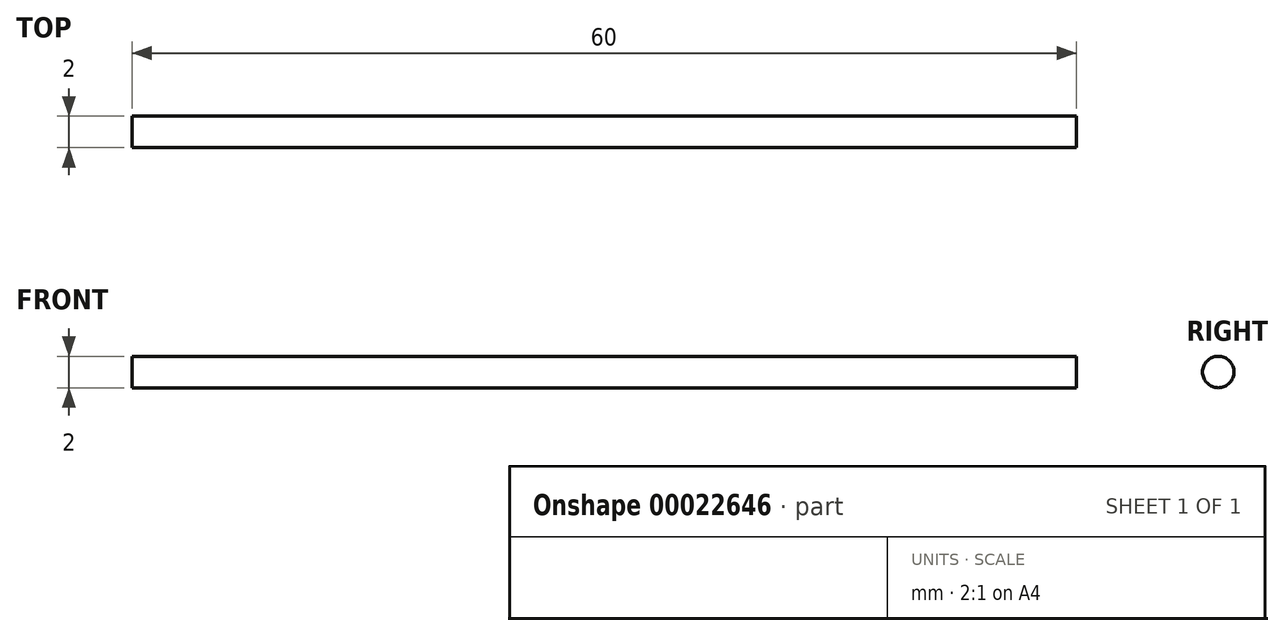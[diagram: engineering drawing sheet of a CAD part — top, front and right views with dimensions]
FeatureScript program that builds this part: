
annotation { "Feature Type Name" : "Feature", "Feature Type Description" : "" }
export const myFeature = defineFeature(function(context is Context, id is Id, definition is map)
    precondition{}
    {
        {
            var Q0;
            Q0=qCreatedBy(makeId("Front.planeOp"),FACE);
            var sketch = newSketch(context, id + "F0", { "sketchPlane" : qUnion([Q0])});
            skLineSegment(sketch, "E0.bottom", {"start": v(-30, 16.32) * mm, "end": v(30, 16.32) * mm});
            skLineSegment(sketch, "E0.top", {"start": v(-30, 15.32) * mm, "end": v(30, 15.32) * mm});
            skLineSegment(sketch, "E0.left", {"start": v(-30, 16.32) * mm, "end": v(-30, 15.32) * mm});
            skLineSegment(sketch, "E0.right", {"start": v(30, 16.32) * mm, "end": v(30, 15.32) * mm});
            skSolve(sketch);
        }
        {
            var Q0;
            Q0=makeQuery(id+"F0.imprint","IMPRINT",FACE,{"disambiguationData":[TD([[makeQuery(id+"F0.imprint","IMPRINT",EDGE,{"derivedFrom":sQuery(id+"F0.wireOp",EDGE,"E0.bottom")}),-1.0]])]});
            var Q1;
            Q1=sQuery(id+"F0.wireOp",EDGE,"E0.top");
            revolve(context, id + "F1", {"entities" : qUnion([Q0]), "axis" : qUnion([Q1]), "revolveType" : RevolveType.FULL});
        }
    });
